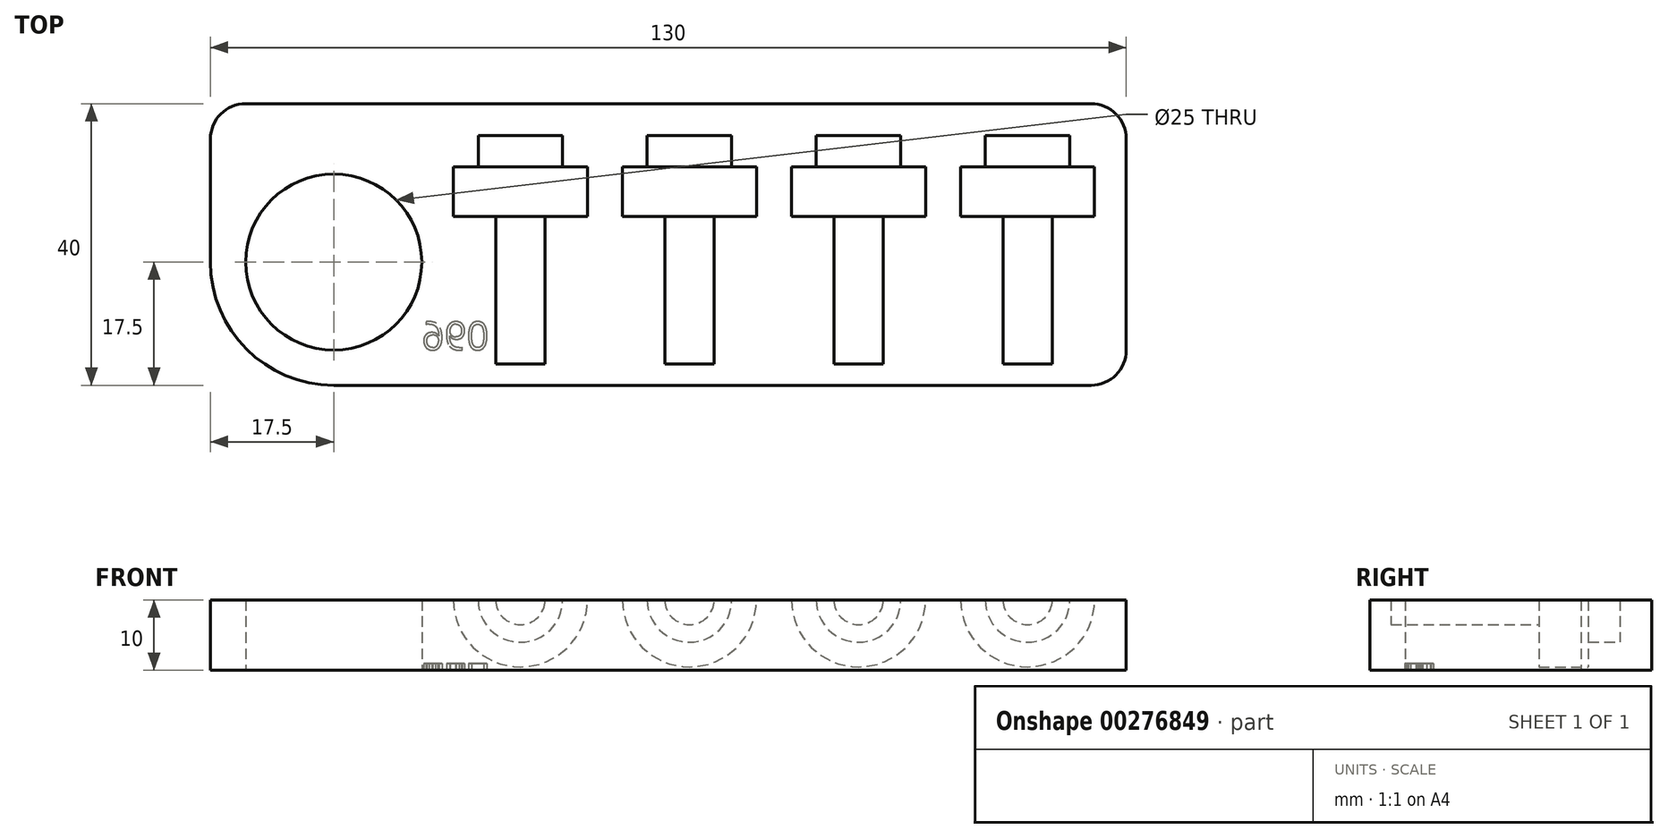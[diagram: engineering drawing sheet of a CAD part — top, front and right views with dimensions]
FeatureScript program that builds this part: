
annotation { "Feature Type Name" : "Feature", "Feature Type Description" : "" }
export const myFeature = defineFeature(function(context is Context, id is Id, definition is map)
    precondition{}
    {
        {
            var Q0;
            Q0=qCreatedBy(makeId("Top.planeOp"),FACE);
            var sketch = newSketch(context, id + "F0", { "sketchPlane" : qUnion([Q0])});
            skLineSegment(sketch, "E0.bottom", {"start": v(17.5, 0) * mm, "end": v(125, 0) * mm});
            skLineSegment(sketch, "E0.top", {"start": v(5, 40) * mm, "end": v(125, 40) * mm});
            skLineSegment(sketch, "E0.left", {"start": v(0, 17.5) * mm, "end": v(0, 35) * mm});
            skLineSegment(sketch, "E0.right", {"start": v(130, 5) * mm, "end": v(130, 35) * mm});
            skLineSegment(sketch, "E1.bottom", {"start": v(0, 0) * mm, "end": v(17.5, 0) * mm, "construction": true});
            skLineSegment(sketch, "E1.top", {"start": v(0, 17.5) * mm, "end": v(17.5, 17.5) * mm, "construction": true});
            skLineSegment(sketch, "E1.left", {"start": v(0, 0) * mm, "end": v(0, 17.5) * mm, "construction": true});
            skLineSegment(sketch, "E1.right", {"start": v(17.5, 0) * mm, "end": v(17.5, 17.5) * mm, "construction": true});
            skCircle(sketch, "E2", {"center": v(17.5, 17.5) * mm, "radius": 12.5 * mm});
            skPoint(sketch, "E3.visualSharp", {"position": v(0, 0) * mm});
            skArc(sketch, "E3.filletArc", {"start": v(0, 17.5) * mm, "mid": v(5.13, 5.13) * mm, "end": v(17.5, 0) * mm});
            skPoint(sketch, "E4.visualSharp", {"position": v(0, 40) * mm});
            skArc(sketch, "E4.filletArc", {"start": v(5, 40) * mm, "mid": v(1.46, 38.54) * mm, "end": v(0, 35) * mm});
            skPoint(sketch, "E5.visualSharp", {"position": v(130, 40) * mm});
            skArc(sketch, "E5.filletArc", {"start": v(130, 35) * mm, "mid": v(128.54, 38.54) * mm, "end": v(125, 40) * mm});
            skPoint(sketch, "E6.visualSharp", {"position": v(130, 0) * mm});
            skArc(sketch, "E6.filletArc", {"start": v(125, 0) * mm, "mid": v(128.54, 1.46) * mm, "end": v(130, 5) * mm});
            skSolve(sketch);
        }
        {
            var Q0;
            Q0=makeQuery(id+"F0.imprint","IMPRINT",FACE,{"disambiguationData":[TD([[makeQuery(id+"F0.imprint","IMPRINT",EDGE,{"derivedFrom":sQuery(id+"F0.wireOp",EDGE,"E0.bottom")}),1.0]])]});
            extrude(context, id + "F1", {"entities" : qUnion([Q0]), "depth" : 10 * mm});
        }
        {
            var Q0;
            Q0=makeQuery(id+"F1.opExtrude","CAP_FACE",FACE,{"disambiguationData":[OSD([sQuery(id+"F0.wireOp",EDGE,"E0.bottom"),sQuery(id+"F0.wireOp",EDGE,"E0.top"),sQuery(id+"F0.wireOp",EDGE,"E0.right"),sQuery(id+"F0.wireOp",EDGE,"E2"),sQuery(id+"F0.wireOp",EDGE,"E3.filletArc"),sQuery(id+"F0.wireOp",EDGE,"E4.filletArc"),sQuery(id+"F0.wireOp",EDGE,"E5.filletArc"),sQuery(id+"F0.wireOp",EDGE,"E6.filletArc")])],"isStart":false});
            var sketch = newSketch(context, id + "F2", { "sketchPlane" : qUnion([Q0])});
            skLineSegment(sketch, "E7.bottom", {"start": v(0, 0) * mm, "end": v(44, 0) * mm, "construction": true});
            skLineSegment(sketch, "E7.top", {"start": v(0, 3) * mm, "end": v(44, 3) * mm, "construction": true});
            skLineSegment(sketch, "E7.left", {"start": v(0, 0) * mm, "end": v(0, 3) * mm, "construction": true});
            skLineSegment(sketch, "E7.right", {"start": v(44, 0) * mm, "end": v(44, 3) * mm, "construction": true});
            skLineSegment(sketch, "E8", {"start": v(44, 3) * mm, "end": v(68, 3) * mm, "construction": true});
            skLineSegment(sketch, "E9", {"start": v(68, 3) * mm, "end": v(92, 3) * mm, "construction": true});
            skLineSegment(sketch, "E10", {"start": v(92, 3) * mm, "end": v(116, 3) * mm, "construction": true});
            skLineSegment(sketch, "E11.bottom", {"start": v(44, 3) * mm, "end": v(47.5, 3) * mm});
            skLineSegment(sketch, "E11.left", {"start": v(44, 3) * mm, "end": v(44, 24) * mm});
            skLineSegment(sketch, "E11.right", {"start": v(47.5, 3) * mm, "end": v(47.5, 24) * mm});
            skLineSegment(sketch, "E12.bottom", {"start": v(68, 3) * mm, "end": v(71.5, 3) * mm});
            skLineSegment(sketch, "E12.left", {"start": v(68, 3) * mm, "end": v(68, 24) * mm});
            skLineSegment(sketch, "E12.right", {"start": v(71.5, 3) * mm, "end": v(71.5, 24) * mm});
            skLineSegment(sketch, "E13.bottom", {"start": v(92, 3) * mm, "end": v(95.5, 3) * mm});
            skLineSegment(sketch, "E13.left", {"start": v(92, 3) * mm, "end": v(92, 24) * mm});
            skLineSegment(sketch, "E13.right", {"start": v(95.5, 3) * mm, "end": v(95.5, 24) * mm});
            skLineSegment(sketch, "E14.bottom", {"start": v(116, 3) * mm, "end": v(119.5, 3) * mm});
            skLineSegment(sketch, "E14.left", {"start": v(116, 3) * mm, "end": v(116, 24) * mm});
            skLineSegment(sketch, "E14.right", {"start": v(119.5, 3) * mm, "end": v(119.5, 24) * mm});
            skLineSegment(sketch, "E15.bottom", {"start": v(47.5, 24) * mm, "end": v(53.5, 24) * mm});
            skLineSegment(sketch, "E15.top", {"start": v(50, 31) * mm, "end": v(53.5, 31) * mm});
            skLineSegment(sketch, "E15.left", {"start": v(44, 24) * mm, "end": v(44, 31) * mm});
            skLineSegment(sketch, "E15.right", {"start": v(53.5, 24) * mm, "end": v(53.5, 31) * mm});
            skLineSegment(sketch, "E16.bottom", {"start": v(71.5, 24) * mm, "end": v(77.5, 24) * mm});
            skLineSegment(sketch, "E16.top", {"start": v(74, 31) * mm, "end": v(77.5, 31) * mm});
            skLineSegment(sketch, "E16.left", {"start": v(68, 24) * mm, "end": v(68, 31) * mm});
            skLineSegment(sketch, "E16.right", {"start": v(77.5, 24) * mm, "end": v(77.5, 31) * mm});
            skLineSegment(sketch, "E17.bottom", {"start": v(95.5, 24) * mm, "end": v(101.5, 24) * mm});
            skLineSegment(sketch, "E17.top", {"start": v(98, 31) * mm, "end": v(101.5, 31) * mm});
            skLineSegment(sketch, "E17.left", {"start": v(92, 24) * mm, "end": v(92, 31) * mm});
            skLineSegment(sketch, "E17.right", {"start": v(101.5, 24) * mm, "end": v(101.5, 31) * mm});
            skLineSegment(sketch, "E18.bottom", {"start": v(119.5, 24) * mm, "end": v(125.5, 24) * mm});
            skLineSegment(sketch, "E18.top", {"start": v(122, 31) * mm, "end": v(125.5, 31) * mm});
            skLineSegment(sketch, "E18.left", {"start": v(116, 24) * mm, "end": v(116, 31) * mm});
            skLineSegment(sketch, "E18.right", {"start": v(125.5, 24) * mm, "end": v(125.5, 31) * mm});
            skLineSegment(sketch, "E19.top", {"start": v(44, 35.5) * mm, "end": v(50, 35.5) * mm});
            skLineSegment(sketch, "E19.left", {"start": v(44, 31) * mm, "end": v(44, 35.5) * mm});
            skLineSegment(sketch, "E19.right", {"start": v(50, 31) * mm, "end": v(50, 35.5) * mm});
            skLineSegment(sketch, "E20.top", {"start": v(68, 35.5) * mm, "end": v(74, 35.5) * mm});
            skLineSegment(sketch, "E20.left", {"start": v(68, 31) * mm, "end": v(68, 35.5) * mm});
            skLineSegment(sketch, "E20.right", {"start": v(74, 31) * mm, "end": v(74, 35.5) * mm});
            skLineSegment(sketch, "E21.top", {"start": v(92, 35.5) * mm, "end": v(98, 35.5) * mm});
            skLineSegment(sketch, "E21.left", {"start": v(92, 31) * mm, "end": v(92, 35.5) * mm});
            skLineSegment(sketch, "E21.right", {"start": v(98, 31) * mm, "end": v(98, 35.5) * mm});
            skLineSegment(sketch, "E22.top", {"start": v(116, 35.5) * mm, "end": v(122, 35.5) * mm});
            skLineSegment(sketch, "E22.left", {"start": v(116, 31) * mm, "end": v(116, 35.5) * mm});
            skLineSegment(sketch, "E22.right", {"start": v(122, 31) * mm, "end": v(122, 35.5) * mm});
            skSolve(sketch);
        }
        {
            var Q0;
            Q0=makeQuery(id+"F2.imprint","IMPRINT",FACE,{"disambiguationData":[TD([[makeQuery(id+"F2.imprint","IMPRINT",EDGE,{"derivedFrom":sQuery(id+"F2.wireOp",EDGE,"E11.bottom")}),1.0]])]});
            var Q1;
            Q1=sQuery(id+"F2.wireOp",EDGE,"E11.left");
            revolve(context, id + "F3", {"operationType" : NewBodyOperationType.REMOVE, "entities" : qUnion([Q0]), "axis" : qUnion([Q1]), "revolveType" : RevolveType.FULL, "oppositeDirection" : true});
        }
        {
            var Q0;
            Q0=makeQuery(id+"F2.imprint","IMPRINT",FACE,{"disambiguationData":[TD([[makeQuery(id+"F2.imprint","IMPRINT",EDGE,{"derivedFrom":sQuery(id+"F2.wireOp",EDGE,"E12.bottom")}),1.0]])]});
            var Q1;
            Q1=sQuery(id+"F2.wireOp",EDGE,"E12.left");
            revolve(context, id + "F4", {"operationType" : NewBodyOperationType.REMOVE, "entities" : qUnion([Q0]), "axis" : qUnion([Q1]), "revolveType" : RevolveType.FULL, "oppositeDirection" : true});
        }
        {
            var Q0;
            Q0=makeQuery(id+"F2.imprint","IMPRINT",FACE,{"disambiguationData":[TD([[makeQuery(id+"F2.imprint","IMPRINT",EDGE,{"derivedFrom":sQuery(id+"F2.wireOp",EDGE,"E13.bottom")}),1.0]])]});
            var Q1;
            Q1=sQuery(id+"F2.wireOp",EDGE,"E13.left");
            revolve(context, id + "F5", {"operationType" : NewBodyOperationType.REMOVE, "entities" : qUnion([Q0]), "axis" : qUnion([Q1]), "revolveType" : RevolveType.FULL, "oppositeDirection" : true});
        }
        {
            var Q0;
            Q0=makeQuery(id+"F2.imprint","IMPRINT",FACE,{"disambiguationData":[TD([[makeQuery(id+"F2.imprint","IMPRINT",EDGE,{"derivedFrom":sQuery(id+"F2.wireOp",EDGE,"E14.bottom")}),1.0]])]});
            var Q1;
            Q1=sQuery(id+"F2.wireOp",EDGE,"E14.left");
            revolve(context, id + "F6", {"operationType" : NewBodyOperationType.REMOVE, "entities" : qUnion([Q0]), "axis" : qUnion([Q1]), "revolveType" : RevolveType.FULL, "oppositeDirection" : true});
        }
        {
            var Q0;
            Q0=makeQuery(id+"F1.opExtrude","CAP_FACE",FACE,{"disambiguationData":[OSD([sQuery(id+"F0.wireOp",EDGE,"E0.bottom"),sQuery(id+"F0.wireOp",EDGE,"E0.top"),sQuery(id+"F0.wireOp",EDGE,"E0.left"),sQuery(id+"F0.wireOp",EDGE,"E0.right"),sQuery(id+"F0.wireOp",EDGE,"E2"),sQuery(id+"F0.wireOp",EDGE,"E3.filletArc"),sQuery(id+"F0.wireOp",EDGE,"E4.filletArc"),sQuery(id+"F0.wireOp",EDGE,"E5.filletArc"),sQuery(id+"F0.wireOp",EDGE,"E6.filletArc")])],"isStart":true});
            var sketch = newSketch(context, id + "F7", { "sketchPlane" : qUnion([Q0])});
            skLineSegment(sketch, "E23.bottom", {"start": v(0, 0) * mm, "end": v(30, 0) * mm, "construction": true});
            skLineSegment(sketch, "E23.top", {"start": v(0, -5) * mm, "end": v(30, -5) * mm, "construction": true});
            skLineSegment(sketch, "E23.left", {"start": v(0, 0) * mm, "end": v(0, -5) * mm, "construction": true});
            skLineSegment(sketch, "E23.right", {"start": v(30, 0) * mm, "end": v(30, -5) * mm, "construction": true});
            skText(sketch, "E24", { "text": "960", "fontName": "OpenSans-Regular.ttf"});
            const initialGuessF7  = {"E24": [0.03, -0.009, 1, 0, 0.004]};
            skSetInitialGuess(sketch, initialGuessF7);
            skSolve(sketch);
        }
        {
            var Q0;
            Q0 = qSketchRegion(id + "F7", true);
            extrude(context, id + "F8", {"entities" : qUnion([Q0]), "operationType" : NewBodyOperationType.REMOVE, "oppositeDirection" : true, "depth" : 1 * mm});
        }
    });
